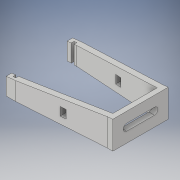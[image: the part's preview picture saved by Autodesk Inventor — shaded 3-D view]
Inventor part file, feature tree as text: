
AUTODESK INVENTOR PART (.ipt)
format: ipt  version: 2019 (Build 230136000, 136)  size: 172,032 bytes
history: native  units: mm
features: extrude x3, sketch x3, mirror x1, draft x1, direct_edit x1, move_body x1
ambient origin geometry x8: Origin, YZ Plane, XZ Plane, XY Plane, X Axis, Y Axis, Z Axis, Center Point
bodies: Solid1 (feature_tree)
feature tree (10):
  extrude  "Extrusion1"  Depth=22.0mm
  mirror  "Mirror1"
  draft  "FaceDraft1"
  extrude  "Extrusion2"  Depth=2.0mm
  extrude  "Extrusion3"  Depth=10.0mm
  direct_edit  "Direct Edit1"
  sketch  "Sketch1"  dims[d0=1.0mm d1=22.0mm]
  sketch  "Sketch2"  dims[d2=3.0mm d3=2.0mm]
  sketch  "Sketch3"  dims[d4=2.0mm d5=10.0mm d6=35.0mm d7=10.0mm d8=0.0mm d9=1.047198mm d10=2.0mm d11=3.0mm d12=2.5mm d13=18.0mm d14=10.0mm d15=0.0mm d16=5.0mm d17=2.5mm d18=10.0mm d19=0.0mm d20=0.0mm d21=0.0mm d22=0.5mm]
  move_body  "Move1"
